# Revit family: Computer-Tower
name_source: partatom
category: Specialty Equipment
units: mm (PartAtom-declared; Revit-internal decimal feet)

## family parameters
Always vertical = Yes
Classification Number = 23.40.70.14.57.11
Cut with Voids When Loaded = No
Enable Cutting in Views = No
Maintain Annotation Orientation = No
Part Type = Normal
Room Calculation Point = No
Round Connector Dimension = Use Diameter
Shared = No
Work Plane-Based = No

## types (1)
- Tower
    Assembly Code = E1010800
    Audio = 5.1
    Construction Details = http://www.arcat.com
    Default Elevation = 0' - 0"
    Description = Desktop PC Tower
    Equipment Accent Color = Plastic - ABS, Silver
    Equipment Color = Plastic - ABS, Grey
    Expected Lifespan (Years) = 10
    Green Building-LEED = http://www.arcat.com
    Keynote = 11680
    Maintenance Schedule (Months) = 6
    Manufacturer = Generic
    Manufacturer Fax = (203) 939-2444
    Manufacturer Website = http://www.arcat.com
    Model = Generic
    Processor = 2.4GHz Quad Core
    Product Data = http://www.arcat.com
    Product Properties = http://www.arcat.com
    Specification = http://www.arcat.com
    Video_Graphics = PCI Express 512MB
    Warranty Duration (Years) = 2

## geometry (parser evidence)
native form markers: Sweep x4
no freeform markers — native parametric forms only
